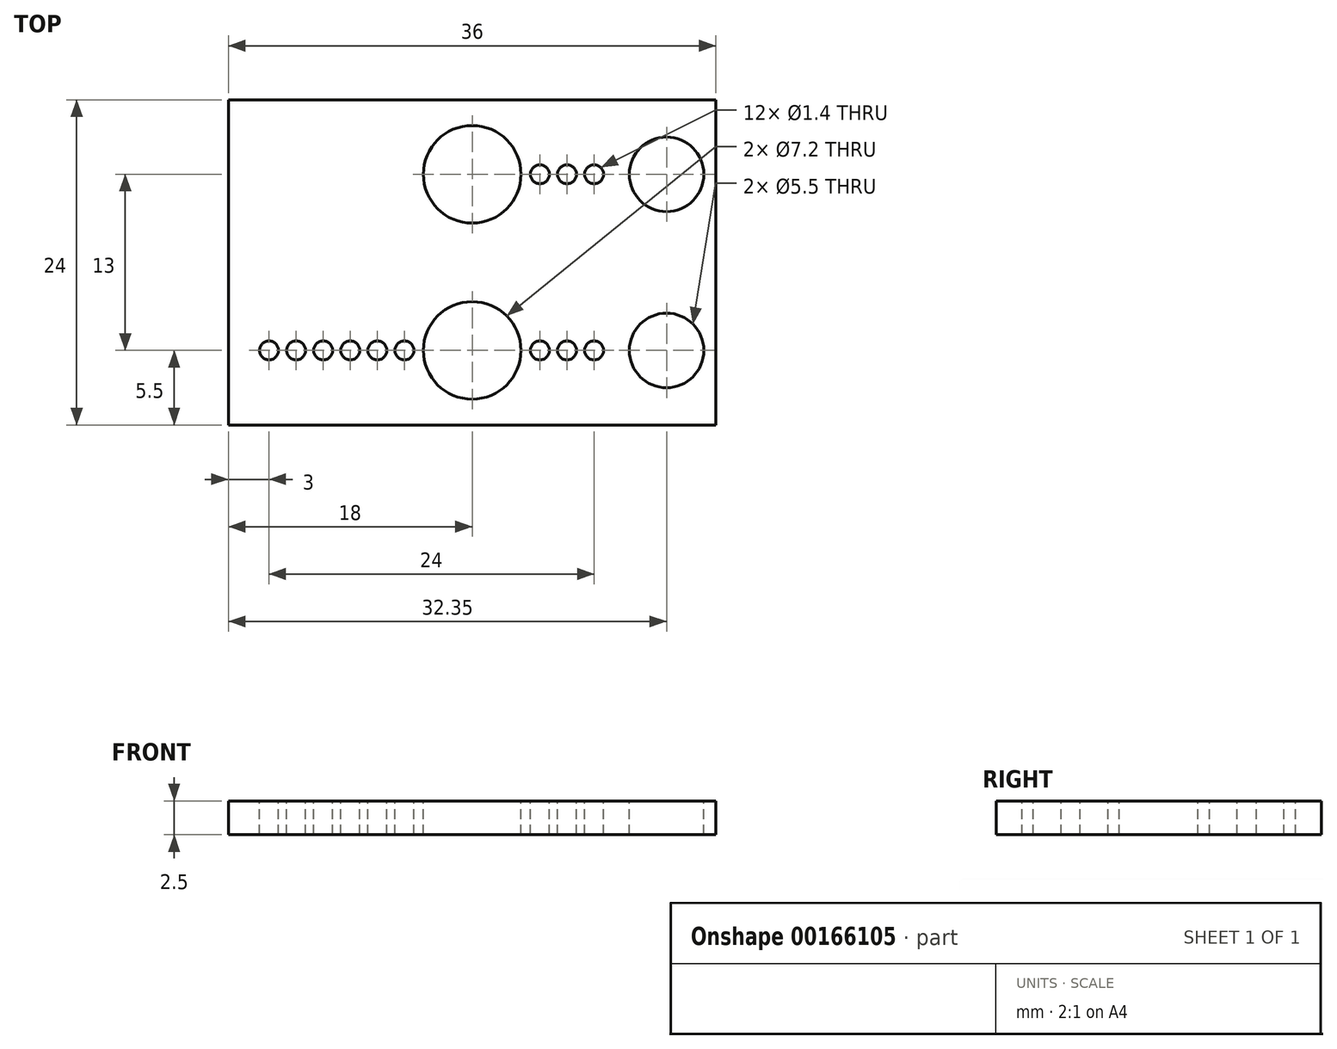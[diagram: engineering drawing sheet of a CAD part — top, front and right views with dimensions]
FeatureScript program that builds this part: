
annotation { "Feature Type Name" : "Feature", "Feature Type Description" : "" }
export const myFeature = defineFeature(function(context is Context, id is Id, definition is map)
    precondition{}
    {
        {
            var Q0;
            Q0=qCreatedBy(makeId("Top.planeOp"),FACE);
            var sketch = newSketch(context, id + "F0", { "sketchPlane" : qUnion([Q0])});
            skLineSegment(sketch, "E0.bottom", {"start": v(-18, 12) * mm, "end": v(18, 12) * mm});
            skLineSegment(sketch, "E0.top", {"start": v(-18, -12) * mm, "end": v(18, -12) * mm});
            skLineSegment(sketch, "E0.left", {"start": v(-18, 12) * mm, "end": v(-18, -12) * mm});
            skLineSegment(sketch, "E0.right", {"start": v(18, 12) * mm, "end": v(18, -12) * mm});
            skPoint(sketch, "E0.middle", {"position": v(0, 0) * mm});
            skCircle(sketch, "E1", {"center": v(0, 6.5) * mm, "radius": 2.6 * mm});
            skCircle(sketch, "E2", {"center": v(0, -6.5) * mm, "radius": 2.6 * mm});
            skCircle(sketch, "E3", {"center": v(0, -6.5) * mm, "radius": 3.6 * mm});
            skCircle(sketch, "E4", {"center": v(0, 6.5) * mm, "radius": 3.6 * mm});
            skCircle(sketch, "E5", {"center": v(-5, -6.5) * mm, "radius": 0.7 * mm});
            skCircle(sketch, "E6", {"center": v(-9, -6.5) * mm, "radius": 0.7 * mm});
            skCircle(sketch, "E7", {"center": v(-11, -6.5) * mm, "radius": 0.7 * mm});
            skCircle(sketch, "E8", {"center": v(-13, -6.5) * mm, "radius": 0.7 * mm});
            skCircle(sketch, "E9", {"center": v(-15, -6.5) * mm, "radius": 0.7 * mm});
            skCircle(sketch, "E10", {"center": v(-7, -6.5) * mm, "radius": 0.7 * mm});
            skLineSegment(sketch, "E11", {"start": v(-18, -6.5) * mm, "end": v(0, -6.5) * mm});
            skLineSegment(sketch, "E12", {"start": v(0, -6.5) * mm, "end": v(18, -6.5) * mm});
            skLineSegment(sketch, "E13", {"start": v(0, 6.5) * mm, "end": v(18, 6.5) * mm});
            skCircle(sketch, "E14", {"center": v(-14.35, -6.5) * mm, "radius": 2.75 * mm});
            skLineSegment(sketch, "E15", {"start": v(-14.51, -3.75) * mm, "end": v(-0.21, -2.9) * mm});
            skLineSegment(sketch, "E16", {"start": v(-14.51, -9.25) * mm, "end": v(-0.21, -10.1) * mm});
            skCircle(sketch, "E17", {"center": v(5, -6.5) * mm, "radius": 0.7 * mm});
            skCircle(sketch, "E18", {"center": v(7, -6.5) * mm, "radius": 0.7 * mm});
            skCircle(sketch, "E19", {"center": v(9, -6.5) * mm, "radius": 0.7 * mm});
            skCircle(sketch, "E20", {"center": v(11, -6.5) * mm, "radius": 0.7 * mm});
            skCircle(sketch, "E21", {"center": v(13, -6.5) * mm, "radius": 0.7 * mm});
            skCircle(sketch, "E22", {"center": v(15, -6.5) * mm, "radius": 0.7 * mm});
            skCircle(sketch, "E23", {"center": v(14.35, -6.5) * mm, "radius": 2.75 * mm});
            skLineSegment(sketch, "E24", {"start": v(0.21, -2.9) * mm, "end": v(14.51, -3.75) * mm});
            skLineSegment(sketch, "E25", {"start": v(0.21, -10.1) * mm, "end": v(14.51, -9.25) * mm});
            skCircle(sketch, "E26", {"center": v(14.35, 6.5) * mm, "radius": 2.75 * mm});
            skCircle(sketch, "E27", {"center": v(5, 6.5) * mm, "radius": 0.7 * mm});
            skCircle(sketch, "E28", {"center": v(7, 6.5) * mm, "radius": 0.7 * mm});
            skCircle(sketch, "E29", {"center": v(9, 6.5) * mm, "radius": 0.7 * mm});
            skCircle(sketch, "E30", {"center": v(11, 6.5) * mm, "radius": 0.7 * mm});
            skCircle(sketch, "E31", {"center": v(13, 6.5) * mm, "radius": 0.7 * mm});
            skCircle(sketch, "E32", {"center": v(15, 6.5) * mm, "radius": 0.7 * mm});
            skLineSegment(sketch, "E33", {"start": v(0.21, 10.1) * mm, "end": v(14.51, 9.25) * mm});
            skLineSegment(sketch, "E34", {"start": v(0.21, 2.9) * mm, "end": v(14.51, 3.75) * mm});
            skSolve(sketch);
        }
        {
            var Q0;
            {var subQ17=sQuery(id+"F0.wireOp",EDGE,"E0.bottom");Q0=makeQuery(id+"F0.imprint","IMPRINT",FACE,{"disambiguationData":[TD([[makeQuery(id+"F0.imprint","IMPRINT",EDGE,{"derivedFrom":subQ17}),-1.0]])]});}
            var Q1;
            {var subQ4=sQuery(id+"F0.wireOp",EDGE,"E0.top");Q1=makeQuery(id+"F0.imprint","IMPRINT",FACE,{"disambiguationData":[TD([[makeQuery(id+"F0.imprint","IMPRINT",EDGE,{"derivedFrom":subQ4}),1.0]])]});}
            var Q2;
            {var subQ0=sQuery(id+"F0.wireOp",EDGE,"E11");var subQ1=sQuery(id+"F0.wireOp",EDGE,"E8");var subQ2=makeQuery(id+"F0.imprint","INTERSECT",VERTEX,{"disambiguationData":[OD(0.0)],"derivedFrom":[subQ1,subQ0]});Q2=makeQuery(id+"F0.imprint","IMPRINT",FACE,{"disambiguationData":[TD([[makeQuery(id+"F0.imprint","IMPRINT",EDGE,{"disambiguationData":[TD([[subQ2,-1.0]])],"derivedFrom":subQ1}),-1.0]])]});}
            var Q3;
            {var subQ0=sQuery(id+"F0.wireOp",EDGE,"E11");var subQ1=sQuery(id+"F0.wireOp",EDGE,"E8");var subQ2=makeQuery(id+"F0.imprint","INTERSECT",VERTEX,{"disambiguationData":[OD(0.0)],"derivedFrom":[subQ1,subQ0]});Q3=makeQuery(id+"F0.imprint","IMPRINT",FACE,{"disambiguationData":[TD([[makeQuery(id+"F0.imprint","IMPRINT",EDGE,{"disambiguationData":[TD([[subQ2,1.0]])],"derivedFrom":subQ1}),-1.0]])]});}
            var Q4;
            {var subQ17=sQuery(id+"F0.wireOp",EDGE,"E15");Q4=makeQuery(id+"F0.imprint","IMPRINT",FACE,{"disambiguationData":[TD([[makeQuery(id+"F0.imprint","IMPRINT",EDGE,{"derivedFrom":subQ17}),-1.0]])]});}
            var Q5;
            {var subQ5=sQuery(id+"F0.wireOp",EDGE,"E16");Q5=makeQuery(id+"F0.imprint","IMPRINT",FACE,{"disambiguationData":[TD([[makeQuery(id+"F0.imprint","IMPRINT",EDGE,{"derivedFrom":subQ5}),1.0]])]});}
            var Q6;
            {var subQ9=sQuery(id+"F0.wireOp",EDGE,"E25");Q6=makeQuery(id+"F0.imprint","IMPRINT",FACE,{"disambiguationData":[TD([[makeQuery(id+"F0.imprint","IMPRINT",EDGE,{"derivedFrom":subQ9}),1.0]])]});}
            var Q7;
            {var subQ16=sQuery(id+"F0.wireOp",EDGE,"E24");Q7=makeQuery(id+"F0.imprint","IMPRINT",FACE,{"disambiguationData":[TD([[makeQuery(id+"F0.imprint","IMPRINT",EDGE,{"derivedFrom":subQ16}),-1.0]])]});}
            var Q8;
            {var subQ7=sQuery(id+"F0.wireOp",EDGE,"E34");Q8=makeQuery(id+"F0.imprint","IMPRINT",FACE,{"disambiguationData":[TD([[makeQuery(id+"F0.imprint","IMPRINT",EDGE,{"derivedFrom":subQ7}),1.0]])]});}
            var Q9;
            {var subQ10=sQuery(id+"F0.wireOp",EDGE,"E33");Q9=makeQuery(id+"F0.imprint","IMPRINT",FACE,{"disambiguationData":[TD([[makeQuery(id+"F0.imprint","IMPRINT",EDGE,{"derivedFrom":subQ10}),-1.0]])]});}
            var Q10;
            {var subQ2=sQuery(id+"F0.wireOp",EDGE,"E30");var subQ4=sQuery(id+"F0.wireOp",EDGE,"E13");var subQ11=makeQuery(id+"F0.imprint","INTERSECT",VERTEX,{"disambiguationData":[OD(1.0)],"derivedFrom":[subQ4,subQ2]});Q10=makeQuery(id+"F0.imprint","IMPRINT",FACE,{"disambiguationData":[TD([[makeQuery(id+"F0.imprint","IMPRINT",EDGE,{"disambiguationData":[TD([[subQ11,-1.0]])],"derivedFrom":subQ4}),-1.0]])]});}
            var Q11;
            {var subQ2=sQuery(id+"F0.wireOp",EDGE,"E13");var subQ9=sQuery(id+"F0.wireOp",EDGE,"E30");var subQ10=makeQuery(id+"F0.imprint","INTERSECT",VERTEX,{"disambiguationData":[OD(1.0)],"derivedFrom":[subQ2,subQ9]});Q11=makeQuery(id+"F0.imprint","IMPRINT",FACE,{"disambiguationData":[TD([[makeQuery(id+"F0.imprint","IMPRINT",EDGE,{"disambiguationData":[TD([[subQ10,-1.0]])],"derivedFrom":subQ2}),1.0]])]});}
            var Q12;
            {var subQ0=sQuery(id+"F0.wireOp",EDGE,"E20");var subQ1=sQuery(id+"F0.wireOp",EDGE,"E12");var subQ2=makeQuery(id+"F0.imprint","INTERSECT",VERTEX,{"disambiguationData":[OD(1.0)],"derivedFrom":[subQ1,subQ0]});Q12=makeQuery(id+"F0.imprint","IMPRINT",FACE,{"disambiguationData":[TD([[makeQuery(id+"F0.imprint","IMPRINT",EDGE,{"disambiguationData":[TD([[subQ2,-1.0]])],"derivedFrom":subQ1}),1.0]])]});}
            var Q13;
            {var subQ0=sQuery(id+"F0.wireOp",EDGE,"E20");var subQ1=sQuery(id+"F0.wireOp",EDGE,"E12");var subQ2=makeQuery(id+"F0.imprint","INTERSECT",VERTEX,{"disambiguationData":[OD(1.0)],"derivedFrom":[subQ1,subQ0]});Q13=makeQuery(id+"F0.imprint","IMPRINT",FACE,{"disambiguationData":[TD([[makeQuery(id+"F0.imprint","IMPRINT",EDGE,{"disambiguationData":[TD([[subQ2,-1.0]])],"derivedFrom":subQ1}),-1.0]])]});}
            extrude(context, id + "F1", {"entities" : qUnion([Q0, Q1, Q2, Q3, Q4, Q5, Q6, Q7, Q8, Q9, Q10, Q11, Q12, Q13]), "oppositeDirection" : true, "depth" : 4 * mm});
        }
        {
            var Q0;
            {var subQ7=sQuery(id+"F0.wireOp",EDGE,"E34");Q0=makeQuery(id+"F0.imprint","IMPRINT",FACE,{"disambiguationData":[TD([[makeQuery(id+"F0.imprint","IMPRINT",EDGE,{"derivedFrom":subQ7}),1.0]])]});}
            var Q1;
            {var subQ10=sQuery(id+"F0.wireOp",EDGE,"E33");Q1=makeQuery(id+"F0.imprint","IMPRINT",FACE,{"disambiguationData":[TD([[makeQuery(id+"F0.imprint","IMPRINT",EDGE,{"derivedFrom":subQ10}),-1.0]])]});}
            var Q2;
            {var subQ0=sQuery(id+"F0.wireOp",EDGE,"E26");var subQ1=sQuery(id+"F0.wireOp",EDGE,"E13");var subQ10=makeQuery(id+"F0.imprint","INTERSECT",VERTEX,{"disambiguationData":[OD(1.0)],"derivedFrom":[subQ1,subQ0]});Q2=makeQuery(id+"F0.imprint","IMPRINT",FACE,{"disambiguationData":[TD([[makeQuery(id+"F0.imprint","IMPRINT",EDGE,{"disambiguationData":[TD([[subQ10,-1.0]])],"derivedFrom":subQ1}),-1.0]])]});}
            var Q3;
            {var subQ0=sQuery(id+"F0.wireOp",EDGE,"E26");var subQ2=sQuery(id+"F0.wireOp",EDGE,"E13");var subQ9=makeQuery(id+"F0.imprint","INTERSECT",VERTEX,{"disambiguationData":[OD(1.0)],"derivedFrom":[subQ2,subQ0]});Q3=makeQuery(id+"F0.imprint","IMPRINT",FACE,{"disambiguationData":[TD([[makeQuery(id+"F0.imprint","IMPRINT",EDGE,{"disambiguationData":[TD([[subQ9,-1.0]])],"derivedFrom":subQ2}),1.0]])]});}
            var Q4;
            {var subQ16=sQuery(id+"F0.wireOp",EDGE,"E24");Q4=makeQuery(id+"F0.imprint","IMPRINT",FACE,{"disambiguationData":[TD([[makeQuery(id+"F0.imprint","IMPRINT",EDGE,{"derivedFrom":subQ16}),-1.0]])]});}
            var Q5;
            {var subQ9=sQuery(id+"F0.wireOp",EDGE,"E25");Q5=makeQuery(id+"F0.imprint","IMPRINT",FACE,{"disambiguationData":[TD([[makeQuery(id+"F0.imprint","IMPRINT",EDGE,{"derivedFrom":subQ9}),1.0]])]});}
            var Q6;
            {var subQ17=sQuery(id+"F0.wireOp",EDGE,"E15");Q6=makeQuery(id+"F0.imprint","IMPRINT",FACE,{"disambiguationData":[TD([[makeQuery(id+"F0.imprint","IMPRINT",EDGE,{"derivedFrom":subQ17}),-1.0]])]});}
            var Q7;
            {var subQ0=sQuery(id+"F0.wireOp",EDGE,"E11");var subQ1=sQuery(id+"F0.wireOp",EDGE,"E8");var subQ2=makeQuery(id+"F0.imprint","INTERSECT",VERTEX,{"disambiguationData":[OD(0.0)],"derivedFrom":[subQ1,subQ0]});Q7=makeQuery(id+"F0.imprint","IMPRINT",FACE,{"disambiguationData":[TD([[makeQuery(id+"F0.imprint","IMPRINT",EDGE,{"disambiguationData":[TD([[subQ2,1.0]])],"derivedFrom":subQ1}),-1.0]])]});}
            var Q8;
            {var subQ0=sQuery(id+"F0.wireOp",EDGE,"E11");var subQ1=sQuery(id+"F0.wireOp",EDGE,"E8");var subQ2=makeQuery(id+"F0.imprint","INTERSECT",VERTEX,{"disambiguationData":[OD(0.0)],"derivedFrom":[subQ1,subQ0]});Q8=makeQuery(id+"F0.imprint","IMPRINT",FACE,{"disambiguationData":[TD([[makeQuery(id+"F0.imprint","IMPRINT",EDGE,{"disambiguationData":[TD([[subQ2,-1.0]])],"derivedFrom":subQ1}),-1.0]])]});}
            var Q9;
            {var subQ5=sQuery(id+"F0.wireOp",EDGE,"E16");Q9=makeQuery(id+"F0.imprint","IMPRINT",FACE,{"disambiguationData":[TD([[makeQuery(id+"F0.imprint","IMPRINT",EDGE,{"derivedFrom":subQ5}),1.0]])]});}
            var Q10;
            {var subQ0=sQuery(id+"F0.wireOp",EDGE,"E20");var subQ1=sQuery(id+"F0.wireOp",EDGE,"E12");var subQ2=makeQuery(id+"F0.imprint","INTERSECT",VERTEX,{"disambiguationData":[OD(1.0)],"derivedFrom":[subQ1,subQ0]});Q10=makeQuery(id+"F0.imprint","IMPRINT",FACE,{"disambiguationData":[TD([[makeQuery(id+"F0.imprint","IMPRINT",EDGE,{"disambiguationData":[TD([[subQ2,-1.0]])],"derivedFrom":subQ1}),1.0]])]});}
            var Q11;
            {var subQ0=sQuery(id+"F0.wireOp",EDGE,"E20");var subQ1=sQuery(id+"F0.wireOp",EDGE,"E12");var subQ2=makeQuery(id+"F0.imprint","INTERSECT",VERTEX,{"disambiguationData":[OD(1.0)],"derivedFrom":[subQ1,subQ0]});Q11=makeQuery(id+"F0.imprint","IMPRINT",FACE,{"disambiguationData":[TD([[makeQuery(id+"F0.imprint","IMPRINT",EDGE,{"disambiguationData":[TD([[subQ2,-1.0]])],"derivedFrom":subQ1}),-1.0]])]});}
            var Q12;
            {var subQ2=sQuery(id+"F0.wireOp",EDGE,"E30");var subQ4=sQuery(id+"F0.wireOp",EDGE,"E13");var subQ11=makeQuery(id+"F0.imprint","INTERSECT",VERTEX,{"disambiguationData":[OD(1.0)],"derivedFrom":[subQ4,subQ2]});Q12=makeQuery(id+"F0.imprint","IMPRINT",FACE,{"disambiguationData":[TD([[makeQuery(id+"F0.imprint","IMPRINT",EDGE,{"disambiguationData":[TD([[subQ11,-1.0]])],"derivedFrom":subQ4}),-1.0]])]});}
            var Q13;
            {var subQ2=sQuery(id+"F0.wireOp",EDGE,"E13");var subQ9=sQuery(id+"F0.wireOp",EDGE,"E30");var subQ10=makeQuery(id+"F0.imprint","INTERSECT",VERTEX,{"disambiguationData":[OD(1.0)],"derivedFrom":[subQ2,subQ9]});Q13=makeQuery(id+"F0.imprint","IMPRINT",FACE,{"disambiguationData":[TD([[makeQuery(id+"F0.imprint","IMPRINT",EDGE,{"disambiguationData":[TD([[subQ10,-1.0]])],"derivedFrom":subQ2}),1.0]])]});}
            var Q14;
            {var subQ1=sQuery(id+"F0.wireOp",EDGE,"E12");var subQ6=sQuery(id+"F0.wireOp",EDGE,"E23");var subQ9=makeQuery(id+"F0.imprint","INTERSECT",VERTEX,{"disambiguationData":[OD(0.0)],"derivedFrom":[subQ1,subQ6]});Q14=makeQuery(id+"F0.imprint","IMPRINT",FACE,{"disambiguationData":[TD([[makeQuery(id+"F0.imprint","IMPRINT",EDGE,{"disambiguationData":[TD([[subQ9,-1.0]])],"derivedFrom":subQ1}),1.0]])]});}
            var Q15;
            {var subQ1=sQuery(id+"F0.wireOp",EDGE,"E12");var subQ6=sQuery(id+"F0.wireOp",EDGE,"E23");var subQ10=makeQuery(id+"F0.imprint","INTERSECT",VERTEX,{"disambiguationData":[OD(0.0)],"derivedFrom":[subQ1,subQ6]});Q15=makeQuery(id+"F0.imprint","IMPRINT",FACE,{"disambiguationData":[TD([[makeQuery(id+"F0.imprint","IMPRINT",EDGE,{"disambiguationData":[TD([[subQ10,-1.0]])],"derivedFrom":subQ1}),-1.0]])]});}
            extrude(context, id + "F2", {"entities" : qUnion([Q0, Q1, Q2, Q3, Q4, Q5, Q6, Q7, Q8, Q9, Q10, Q11, Q12, Q13, Q14, Q15]), "operationType" : NewBodyOperationType.REMOVE, "oppositeDirection" : true, "depth" : 1.5 * mm});
        }
    });
